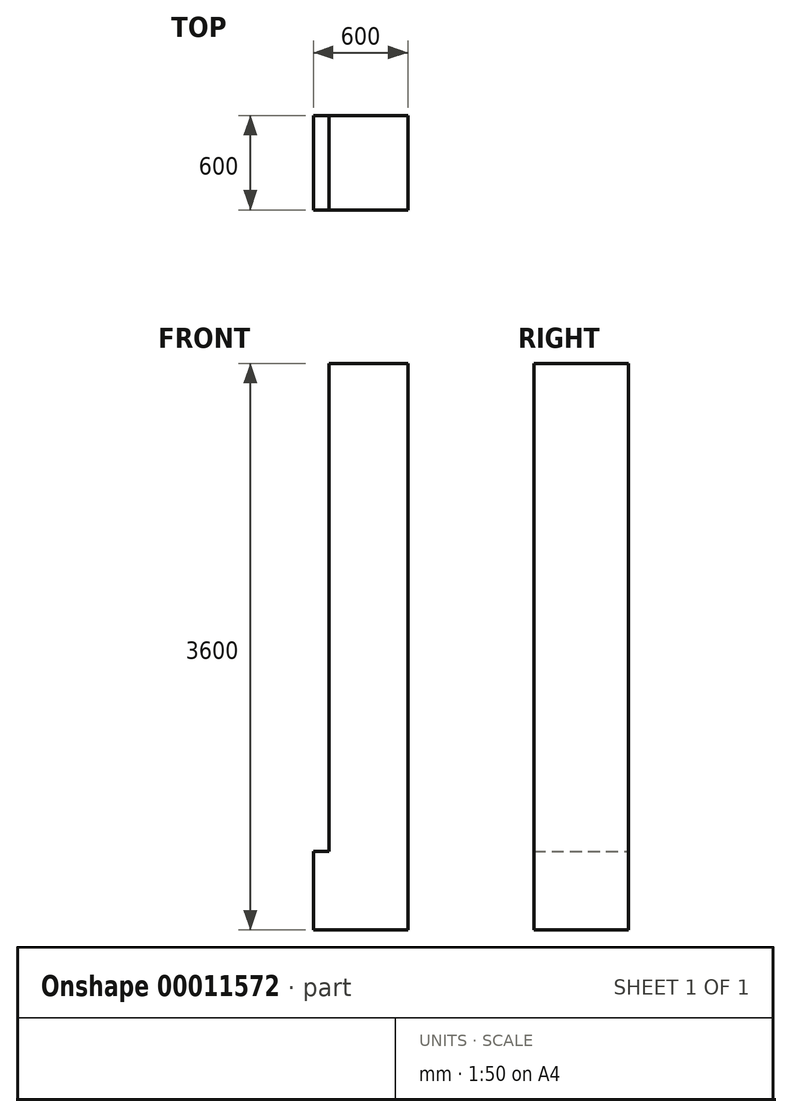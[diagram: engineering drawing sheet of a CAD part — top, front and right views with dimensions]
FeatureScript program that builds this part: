
annotation { "Feature Type Name" : "Feature", "Feature Type Description" : "" }
export const myFeature = defineFeature(function(context is Context, id is Id, definition is map)
    precondition{}
    {
        {
            var Q0;
            Q0=qCreatedBy(makeId("Front.planeOp"),FACE);
            var sketch = newSketch(context, id + "F0", { "sketchPlane" : qUnion([Q0])});
            skLineSegment(sketch, "E0.rect.bottom", {"start": v(-200, 300) * mm, "end": v(300, 300) * mm});
            skLineSegment(sketch, "E0.rect.top", {"start": v(-300, -300) * mm, "end": v(300, -300) * mm});
            skLineSegment(sketch, "E0.rect.left", {"start": v(-300, 200) * mm, "end": v(-300, -300) * mm});
            skLineSegment(sketch, "E0.rect.right", {"start": v(300, 300) * mm, "end": v(300, -300) * mm});
            skPoint(sketch, "E0.rect.middle", {"position": v(0, 0) * mm});
            skLineSegment(sketch, "E1", {"start": v(-300, 200) * mm, "end": v(-200, 200) * mm});
            skLineSegment(sketch, "E2", {"start": v(-200, 200) * mm, "end": v(-200, 300) * mm});
            skPoint(sketch, "E3.orphan", {"position": v(-300, 300) * mm});
            skSolve(sketch);
        }
        {
            var Q0;
            Q0=makeQuery(id+"F0.imprint","IMPRINT",FACE,{"disambiguationData":[TD([[makeQuery(id+"F0.imprint","IMPRINT",EDGE,{"derivedFrom":sQuery(id+"F0.wireOp",EDGE,"E0.rect.bottom")}),-1.0]])]});
            extrude(context, id + "F1", {"entities" : qUnion([Q0]), "endBound" : BoundingType.SYMMETRIC, "depth" : 600 * mm});
        }
        {
            var Q0;
            Q0=makeQuery(id+"F1.opExtrude","SWEPT_FACE",FACE,{"disambiguationData":[OSD([sQuery(id+"F0.wireOp",EDGE,"E0.rect.bottom")])]});
            extrude(context, id + "F2", {"entities" : qUnion([Q0]), "operationType" : NewBodyOperationType.ADD, "depth" : 3000 * mm});
        }
    });
